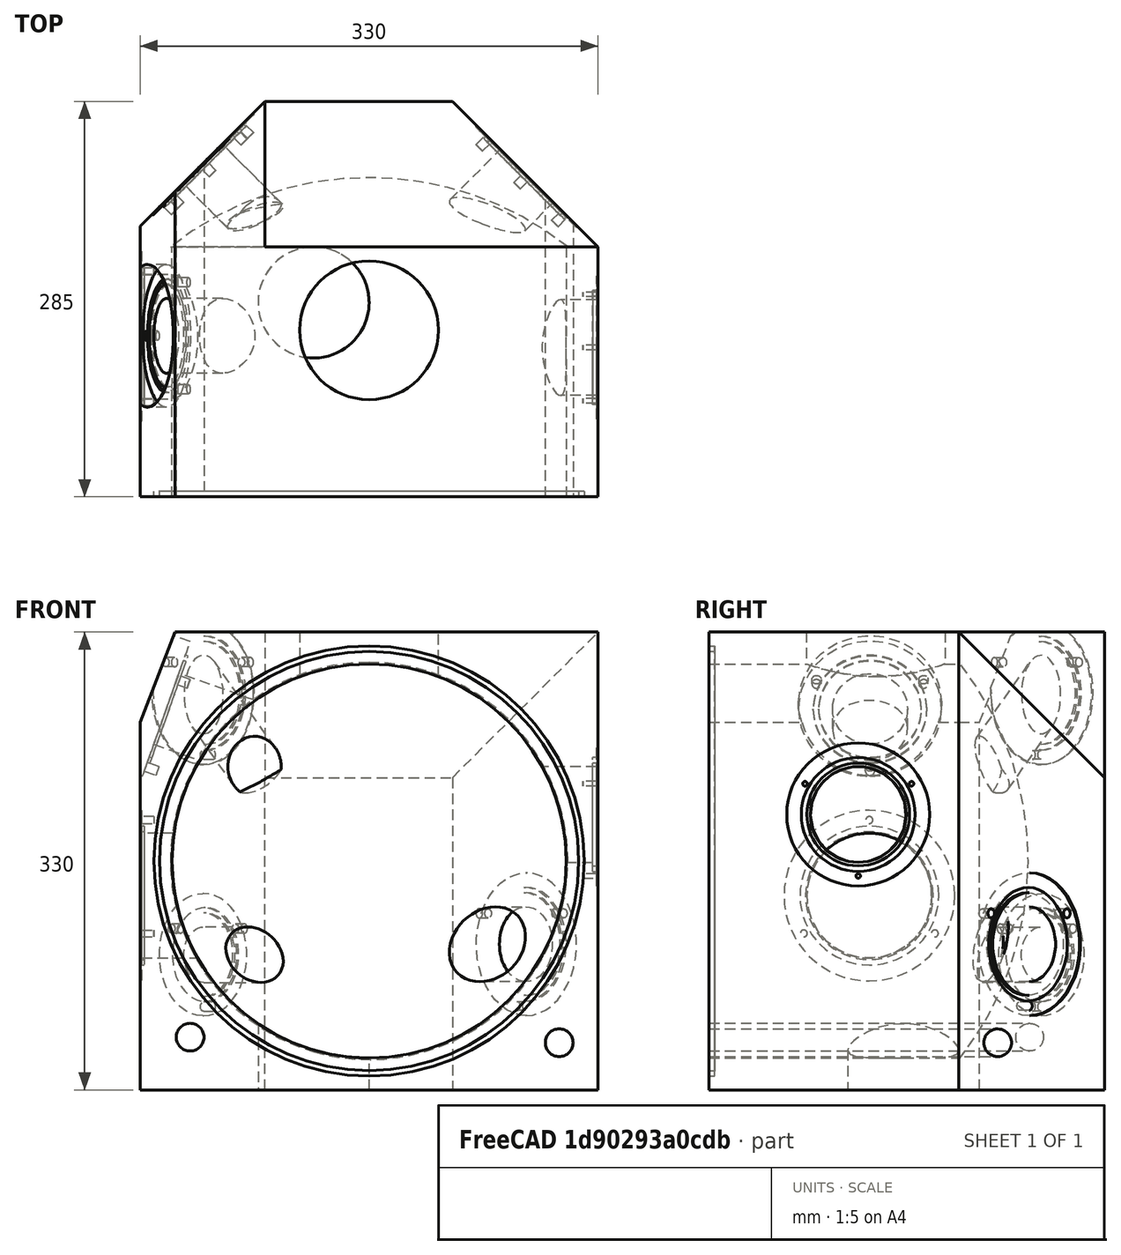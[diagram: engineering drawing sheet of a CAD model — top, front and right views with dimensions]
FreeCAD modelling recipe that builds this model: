
FCSTD DOCUMENT  (FreeCAD 0.20R)
Label: XL30MainChamberModel
License: All rights reserved
LicenseURL: http://en.wikipedia.org/wiki/All_rights_reserved
objects: Part::Cylinder×49, Part::Cut×21, Part::Compound×17, Part::MultiFuse×8, Part::Box×7, Part::Sphere×1
note: 103 computed .brp shape members not serialized (recipe doc carries the construction recipe); baked Part::Feature solids carry a one-line shape summary decoded from their .brp

FEATURE [Part::Box] Box  label="Würfel"
  AttacherType = Attacher::AttachEngine3D
  Height = 330
  Length = 330
  Width = 180
FEATURE [Part::Cylinder] Cylinder  label="Zylinder"
  Angle = 360
  AttacherType = Attacher::AttachEngine3D
  FirstAngle = 0
  Height = 180
  Placement = pos=(165,180,165) rot=(1,0,0;1.5708rad)
  Radius = 142
  SecondAngle = 0
FEATURE [Part::Cut] Cut
  Base = -> Box
  Tool = -> Cylinder
FEATURE [Part::Box] Box001  label="Würfel001"
  AttacherType = Attacher::AttachEngine3D
  Height = 50
  Length = 70
  Placement = pos=(0,0,265) rot=(0,-1,0;1.20428rad)
  Width = 180
FEATURE [Part::Cut] Cut001
  Base = -> Cut
  Tool = -> Box001
FEATURE [Part::Cylinder] Cylinder001  label="Flange100Right_Hole"
  Angle = 360
  AttacherType = Attacher::AttachEngine3D
  FirstAngle = 0
  Height = 50
  Placement = pos=(284,107.5,198.5) rot=(0,1,0;1.5708rad)
  Radius = 34.5
  SecondAngle = 0
FEATURE [Part::Cylinder] Cylinder002  label="Flange100Right_Recess"
  Angle = 360
  AttacherType = Attacher::AttachEngine3D
  FirstAngle = 0
  Height = 1
  Placement = pos=(329,107.5,198.5) rot=(0,1,0;1.5708rad)
  Radius = 51.5
  SecondAngle = 0
FEATURE [Part::Cylinder] Cylinder003  label="Zylinder001"
  Angle = 360
  AttacherType = Attacher::AttachEngine3D
  FirstAngle = 0
  Height = 3
  Radius = 41
  SecondAngle = 0
FEATURE [Part::Cylinder] Cylinder004  label="Zylinder002"
  Angle = 360
  AttacherType = Attacher::AttachEngine3D
  FirstAngle = 0
  Height = 3
  Radius = 37
  SecondAngle = 0
FEATURE [Part::Cut] Cut002
  Base = -> Cylinder003
  Placement = pos=(326,107.5,198.5) rot=(0,1,0;1.5708rad)
  Tool = -> Cylinder004
FEATURE [Part::Cylinder] Cylinder005  label="Zylinder003"
  Angle = 360
  AttacherType = Attacher::AttachEngine3D
  FirstAngle = 0
  Height = 10
  Placement = pos=(0,0,-44.3) rot=(0,1,0;1.5708rad)
  Radius = 1.65
  SecondAngle = 0
FEATURE [Part::Cylinder] Cylinder006  label="Zylinder004"
  Angle = 360
  AttacherType = Attacher::AttachEngine3D
  FirstAngle = 0
  Height = 10
  Placement = pos=(0,0,-44.3) rot=(0,1,0;1.5708rad)
  Radius = 1.65
  SecondAngle = 0
FEATURE [Part::Cylinder] Cylinder007  label="Zylinder005"
  Angle = 360
  AttacherType = Attacher::AttachEngine3D
  FirstAngle = 0
  Height = 10
  Placement = pos=(0,0,-44.3) rot=(0,1,0;1.5708rad)
  Radius = 1.65
  SecondAngle = 0
FEATURE [Part::Compound] Compound001
  Links = -> [Cylinder006]
  Placement = pos=(0,0,0) rot=(1,0,0;2.0944rad)
FEATURE [Part::Compound] Compound002
  Links = -> [Cylinder007]
  Placement = pos=(0,0,0) rot=(1,0,0;4.18879rad)
FEATURE [Part::Compound] Compound003  label="M4 holes flange right"
  Links = -> [Cylinder005,Compound001,Compound002]
  Placement = pos=(319,107.5,198.5) rot=(0,0,1;0rad)
FEATURE [Part::MultiFuse] Fusion
  Shapes = -> [Cylinder001,Cylinder002,Cut002,Compound003]
FEATURE [Part::Cut] Cut003
  Base = -> Cut001
  Tool = -> Fusion
FEATURE [Part::Cylinder] Cylinder008  label="Flange120LeftLow_Recess"
  Angle = 360
  AttacherType = Attacher::AttachEngine3D
  FirstAngle = 0
  Height = 1
  Placement = pos=(0,0,-1) rot=(0,0,1;0rad)
  Radius = 61.5
  SecondAngle = 0
FEATURE [Part::Cylinder] Cylinder009  label="Zylinder006"
  Angle = 360
  AttacherType = Attacher::AttachEngine3D
  FirstAngle = 0
  Height = 60
  Placement = pos=(0,0,-45) rot=(0,0,1;0rad)
  Radius = 45
  SecondAngle = 0
FEATURE [Part::Cylinder] Cylinder010  label="Zylinder007"
  Angle = 360
  AttacherType = Attacher::AttachEngine3D
  FirstAngle = 0
  Height = 2
  Placement = pos=(0,0,-3) rot=(0,0,1;0rad)
  Radius = 50
  SecondAngle = 0
FEATURE [Part::Cylinder] Cylinder011  label="Zylinder008"
  Angle = 360
  AttacherType = Attacher::AttachEngine3D
  FirstAngle = 0
  Height = 2
  Placement = pos=(0,0,-3) rot=(0,0,1;0rad)
  Radius = 46
  SecondAngle = 0
FEATURE [Part::Cut] Cut004
  Base = -> Cylinder010
  Tool = -> Cylinder011
FEATURE [Part::Cylinder] Cylinder012  label="Zylinder009"
  Angle = 360
  AttacherType = Attacher::AttachEngine3D
  FirstAngle = 0
  Height = 10
  Placement = pos=(54.5,0,-10) rot=(0,0,1;0rad)
  Radius = 2.5
  SecondAngle = 0
FEATURE [Part::Cylinder] Cylinder013  label="Zylinder010"
  Angle = 360
  AttacherType = Attacher::AttachEngine3D
  FirstAngle = 0
  Height = 10
  Placement = pos=(54.5,0,-10) rot=(0,0,1;0rad)
  Radius = 2.5
  SecondAngle = 0
FEATURE [Part::Cylinder] Cylinder015  label="Zylinder012"
  Angle = 360
  AttacherType = Attacher::AttachEngine3D
  FirstAngle = 0
  Height = 10
  Placement = pos=(54.5,0,-10) rot=(0,0,1;0rad)
  Radius = 2.5
  SecondAngle = 0
FEATURE [Part::Compound] Compound
  Links = -> [Cylinder013]
  Placement = pos=(0,0,0) rot=(0,0,1;2.0944rad)
FEATURE [Part::Compound] Compound004
  Links = -> [Cylinder015]
  Placement = pos=(0,0,0) rot=(0,0,1;4.18879rad)
FEATURE [Part::MultiFuse] Fusion001  label="Flange120LeftLow"
  Placement = pos=(0,115.5,140) rot=(0,-1,0;1.5708rad)
  Shapes = -> [Cylinder008,Cylinder009,Cut004,Cylinder012,Compound,Compound004]
FEATURE [Part::Cut] Cut005
  Base = -> Cut003
  Tool = -> Fusion001
FEATURE [Part::Cylinder] Cylinder016  label="Zylinder013"
  Angle = 360
  AttacherType = Attacher::AttachEngine3D
  FirstAngle = 0
  Height = 100
  Placement = pos=(0,0,0) rot=(0,1,0;1.5708rad)
  Radius = 27
  SecondAngle = 0
FEATURE [Part::Cylinder] Cylinder017  label="Zylinder014"
  Angle = 360
  AttacherType = Attacher::AttachEngine3D
  FirstAngle = 0
  Height = 100
  Placement = pos=(-99,0,0) rot=(0,1,0;1.5708rad)
  Radius = 51.5
  SecondAngle = 0
FEATURE [Part::Cylinder] Cylinder018  label="Zylinder015"
  Angle = 360
  AttacherType = Attacher::AttachEngine3D
  FirstAngle = 0
  Height = 2
  Radius = 41
  SecondAngle = 0
FEATURE [Part::Cylinder] Cylinder019  label="Zylinder016"
  Angle = 360
  AttacherType = Attacher::AttachEngine3D
  FirstAngle = 0
  Height = 2
  Radius = 37
  SecondAngle = 0
FEATURE [Part::Cut] Cut006
  Base = -> Cylinder018
  Placement = pos=(1,0,0) rot=(0,1,0;1.5708rad)
  Tool = -> Cylinder019
FEATURE [Part::Cylinder] Cylinder020  label="Zylinder017"
  Angle = 360
  AttacherType = Attacher::AttachEngine3D
  FirstAngle = 0
  Height = 10
  Placement = pos=(0,0,-44.5) rot=(0,1,0;1.5708rad)
  Radius = 3.3
  SecondAngle = 0
FEATURE [Part::Cylinder] Cylinder021  label="Zylinder018"
  Angle = 360
  AttacherType = Attacher::AttachEngine3D
  FirstAngle = 0
  Height = 10
  Placement = pos=(0,0,-44.5) rot=(0,1,0;1.5708rad)
  Radius = 3.3
  SecondAngle = 0
FEATURE [Part::Cylinder] Cylinder022  label="Zylinder019"
  Angle = 360
  AttacherType = Attacher::AttachEngine3D
  FirstAngle = 0
  Height = 10
  Placement = pos=(0,0,-44.5) rot=(0,1,0;1.5708rad)
  Radius = 3.3
  SecondAngle = 0
FEATURE [Part::Compound] Compound005
  Links = -> [Cylinder021]
  Placement = pos=(0,0,0) rot=(1,0,0;2.0944rad)
FEATURE [Part::Compound] Compound006
  Links = -> [Cylinder022]
  Placement = pos=(0,0,0) rot=(1,0,0;4.18879rad)
FEATURE [Part::MultiFuse] Fusion002  label="FlangeSEDetector"
  Placement = pos=(18,116,275) rot=(0,1,0;0.340339rad)
  Shapes = -> [Cylinder016,Cylinder017,Cut006,Cylinder020,Compound005,Compound006]
FEATURE [Part::Cut] Cut007
  Base = -> Cut005
  Tool = -> Fusion002
FEATURE [Part::Cylinder] Cylinder023  label="ODPHoleNoFlange"
  Angle = 360
  AttacherType = Attacher::AttachEngine3D
  FirstAngle = 0
  Height = 50
  Placement = pos=(125,140,0) rot=(0,0,1;0rad)
  Radius = 40
  SecondAngle = 0
FEATURE [Part::Cut] Cut008
  Base = -> Cut007
  Tool = -> Cylinder023
FEATURE [Part::Cylinder] Cylinder024  label="EGunHoleWithoutFlange"
  Angle = 360
  AttacherType = Attacher::AttachEngine3D
  FirstAngle = 0
  Height = 50
  Placement = pos=(165,120,280) rot=(0,0,1;0rad)
  Radius = 50
  SecondAngle = 0
FEATURE [Part::Cut] Cut009  label="FrontChamber"
  Base = -> Cut008
  Tool = -> Cylinder024
FEATURE [Part::Box] Box002  label="Würfel002"
  AttacherType = Attacher::AttachEngine3D
  Height = 330
  Length = 330
  Width = 105
FEATURE [Part::Box] Box003  label="Würfel003"
  AttacherType = Attacher::AttachEngine3D
  Height = 330
  Length = 150
  Placement = pos=(330,0,0) rot=(0,0,1;0.785398rad)
  Width = 200
FEATURE [Part::Box] Box004  label="Würfel004"
  AttacherType = Attacher::AttachEngine3D
  Height = 150
  Length = 240
  Placement = pos=(90,0,330) rot=(-1,0,0;0.785398rad)
  Width = 150
FEATURE [Part::Box] Box005  label="Würfel005"
  AttacherType = Attacher::AttachEngine3D
  Height = 330
  Length = 150
  Placement = pos=(0,15,0) rot=(0,0,1;0.785398rad)
  Width = 100
FEATURE [Part::Box] Box007  label="Würfel007"
  AttacherType = Attacher::AttachEngine3D
  Height = 50
  Length = 70
  Placement = pos=(0,0,265) rot=(0,-1,0;1.20428rad)
  Width = 180
FEATURE [Part::MultiFuse] Fusion003
  Shapes = -> [Box005,Box003,Box004,Box007]
FEATURE [Part::Cut] Cut010
  Base = -> Box002
  Placement = pos=(0,180,0) rot=(0,0,1;0rad)
  Tool = -> Fusion003
FEATURE [Part::Cylinder] Cylinder025  label="Zylinder020"
  Angle = 360
  AttacherType = Attacher::AttachEngine3D
  FirstAngle = 0
  Height = 100
  Placement = pos=(0,0,0) rot=(0,1,0;1.5708rad)
  Radius = 27
  SecondAngle = 0
FEATURE [Part::Cylinder] Cylinder026  label="Zylinder021"
  Angle = 360
  AttacherType = Attacher::AttachEngine3D
  FirstAngle = 0
  Height = 100
  Placement = pos=(-99,0,0) rot=(0,1,0;1.5708rad)
  Radius = 51.5
  SecondAngle = 0
FEATURE [Part::Cylinder] Cylinder027  label="Zylinder022"
  Angle = 360
  AttacherType = Attacher::AttachEngine3D
  FirstAngle = 0
  Height = 2
  Radius = 41
  SecondAngle = 0
FEATURE [Part::Cylinder] Cylinder028  label="Zylinder023"
  Angle = 360
  AttacherType = Attacher::AttachEngine3D
  FirstAngle = 0
  Height = 2
  Radius = 37
  SecondAngle = 0
FEATURE [Part::Cut] Cut011
  Base = -> Cylinder027
  Placement = pos=(1,0,0) rot=(0,1,0;1.5708rad)
  Tool = -> Cylinder028
FEATURE [Part::Cylinder] Cylinder029  label="Zylinder024"
  Angle = 360
  AttacherType = Attacher::AttachEngine3D
  FirstAngle = 0
  Height = 10
  Placement = pos=(0,0,-44.5) rot=(0,1,0;1.5708rad)
  Radius = 3.3
  SecondAngle = 0
FEATURE [Part::Cylinder] Cylinder030  label="Zylinder025"
  Angle = 360
  AttacherType = Attacher::AttachEngine3D
  FirstAngle = 0
  Height = 10
  Placement = pos=(0,0,-44.5) rot=(0,1,0;1.5708rad)
  Radius = 3.3
  SecondAngle = 0
FEATURE [Part::Compound] Compound007
  Links = -> [Cylinder030]
  Placement = pos=(0,0,0) rot=(1,0,0;2.0944rad)
FEATURE [Part::Cylinder] Cylinder031  label="Zylinder026"
  Angle = 360
  AttacherType = Attacher::AttachEngine3D
  FirstAngle = 0
  Height = 10
  Placement = pos=(0,0,-44.5) rot=(0,1,0;1.5708rad)
  Radius = 3.3
  SecondAngle = 0
FEATURE [Part::Compound] Compound008
  Links = -> [Cylinder031]
  Placement = pos=(0,0,0) rot=(1,0,0;4.18879rad)
FEATURE [Part::MultiFuse] Fusion004  label="BSEFlange"
  Placement = pos=(278.7,231.3,105) rot=(0,0,1;3.92699rad)
  Shapes = -> [Cylinder025,Cylinder026,Cut011,Cylinder029,Compound007,Compound008]
FEATURE [Part::Compound] Compound009  label="BSEFlange1"
  Links = -> [Fusion004]
FEATURE [Part::Cut] Cut012
  Base = -> Cut010
  Tool = -> Compound009
FEATURE [Part::Cylinder] Cylinder032  label="Zylinder027"
  Angle = 360
  AttacherType = Attacher::AttachEngine3D
  FirstAngle = 0
  Height = 100
  Placement = pos=(0,0,0) rot=(0,1,0;1.5708rad)
  Radius = 20
  SecondAngle = 0
FEATURE [Part::Cylinder] Cylinder033  label="Zylinder028"
  Angle = 360
  AttacherType = Attacher::AttachEngine3D
  FirstAngle = 0
  Height = 100
  Placement = pos=(-99,0,0) rot=(0,1,0;1.5708rad)
  Radius = 44
  SecondAngle = 0
FEATURE [Part::Cylinder] Cylinder034  label="Zylinder029"
  Angle = 360
  AttacherType = Attacher::AttachEngine3D
  FirstAngle = 0
  Height = 2
  Radius = 33.8
  SecondAngle = 0
FEATURE [Part::Cylinder] Cylinder035  label="Zylinder030"
  Angle = 360
  AttacherType = Attacher::AttachEngine3D
  FirstAngle = 0
  Height = 2
  Radius = 30
  SecondAngle = 0
FEATURE [Part::Cut] Cut013
  Base = -> Cylinder034
  Placement = pos=(1,0,0) rot=(0,1,0;1.5708rad)
  Tool = -> Cylinder035
FEATURE [Part::Cylinder] Cylinder036  label="Zylinder031"
  Angle = 360
  AttacherType = Attacher::AttachEngine3D
  FirstAngle = 0
  Height = 10
  Placement = pos=(0,0,-37.5) rot=(0,1,0;1.5708rad)
  Radius = 3.3
  SecondAngle = 0
FEATURE [Part::Cylinder] Cylinder037  label="Zylinder032"
  Angle = 360
  AttacherType = Attacher::AttachEngine3D
  FirstAngle = 0
  Height = 10
  Placement = pos=(0,0,-37.5) rot=(0,1,0;1.5708rad)
  Radius = 3.3
  SecondAngle = 0
FEATURE [Part::Compound] Compound010
  Links = -> [Cylinder037]
  Placement = pos=(0,0,0) rot=(1,0,0;2.0944rad)
FEATURE [Part::Cylinder] Cylinder038  label="Zylinder033"
  Angle = 360
  AttacherType = Attacher::AttachEngine3D
  FirstAngle = 0
  Height = 10
  Placement = pos=(0,0,-37.5) rot=(0,1,0;1.5708rad)
  Radius = 3.3
  SecondAngle = 0
FEATURE [Part::Compound] Compound011
  Links = -> [Cylinder038]
  Placement = pos=(0,0,0) rot=(1,0,0;4.18879rad)
FEATURE [Part::MultiFuse] Fusion005  label="BSEFlange003"
  Placement = pos=(0,0,0) rot=(0,0,-1;0.785398rad)
  Shapes = -> [Cylinder032,Cylinder033,Cut013,Cylinder036,Compound010,Compound011]
FEATURE [Part::Compound] Compound012  label="SideFlangeBack2Low"
  Links = -> [Fusion005]
  Placement = pos=(45,240,97.5) rot=(0,0,1;0rad)
FEATURE [Part::Cut] Cut014
  Base = -> Cut012
  Tool = -> Compound012
FEATURE [Part::Cylinder] Cylinder039  label="Zylinder034"
  Angle = 360
  AttacherType = Attacher::AttachEngine3D
  FirstAngle = 0
  Height = 110
  Placement = pos=(-20,0,20) rot=(0,1,0;2.35619rad)
  Radius = 20
  SecondAngle = 0
FEATURE [Part::Cylinder] Cylinder040  label="Zylinder035"
  Angle = 360
  AttacherType = Attacher::AttachEngine3D
  FirstAngle = 0
  Height = 100
  Placement = pos=(-99,0,0) rot=(0,1,0;1.5708rad)
  Radius = 51.5
  SecondAngle = 0
FEATURE [Part::Cylinder] Cylinder041  label="Zylinder036"
  Angle = 360
  AttacherType = Attacher::AttachEngine3D
  FirstAngle = 0
  Height = 2
  Radius = 41
  SecondAngle = 0
FEATURE [Part::Cylinder] Cylinder042  label="Zylinder037"
  Angle = 360
  AttacherType = Attacher::AttachEngine3D
  FirstAngle = 0
  Height = 2
  Radius = 37
  SecondAngle = 0
FEATURE [Part::Cut] Cut015
  Base = -> Cylinder041
  Placement = pos=(1,0,0) rot=(0,1,0;1.5708rad)
  Tool = -> Cylinder042
FEATURE [Part::Cylinder] Cylinder043  label="Zylinder038"
  Angle = 360
  AttacherType = Attacher::AttachEngine3D
  FirstAngle = 0
  Height = 10
  Placement = pos=(0,0,-44.5) rot=(0,1,0;1.5708rad)
  Radius = 3.3
  SecondAngle = 0
FEATURE [Part::Cylinder] Cylinder044  label="Zylinder039"
  Angle = 360
  AttacherType = Attacher::AttachEngine3D
  FirstAngle = 0
  Height = 10
  Placement = pos=(0,0,-44.5) rot=(0,1,0;1.5708rad)
  Radius = 3.3
  SecondAngle = 0
FEATURE [Part::Compound] Compound013
  Links = -> [Cylinder044]
  Placement = pos=(0,0,0) rot=(1,0,0;2.0944rad)
FEATURE [Part::Cylinder] Cylinder045  label="Zylinder040"
  Angle = 360
  AttacherType = Attacher::AttachEngine3D
  FirstAngle = 0
  Height = 10
  Placement = pos=(0,0,-44.5) rot=(0,1,0;1.5708rad)
  Radius = 3.3
  SecondAngle = 0
FEATURE [Part::Compound] Compound014
  Links = -> [Cylinder045]
  Placement = pos=(0,0,0) rot=(1,0,0;4.18879rad)
FEATURE [Part::MultiFuse] Fusion006  label="BSEFlange005"
  Placement = pos=(0,0,286) rot=(0,0,-1;0.785398rad)
  Shapes = -> [Cylinder039,Cylinder040,Cut015,Cylinder043,Compound013,Compound014]
FEATURE [Part::Compound] Compound015  label="BackTopFlange100"
  Links = -> [Fusion006]
  Placement = pos=(45,240,0) rot=(0,0,1;0rad)
FEATURE [Part::Cut] Cut016  label="BackChamber01"
  Base = -> Cut014
  Tool = -> Compound015
FEATURE [Part::Cylinder] Cylinder046  label="Zylinder041"
  Angle = 360
  AttacherType = Attacher::AttachEngine3D
  FirstAngle = 0
  Height = 800
  Placement = pos=(36,500,38) rot=(1,0,0;1.5708rad)
  Radius = 10
  SecondAngle = 0
FEATURE [Part::Cylinder] Cylinder047  label="Zylinder042"
  Angle = 360
  AttacherType = Attacher::AttachEngine3D
  FirstAngle = 0
  Height = 800
  Placement = pos=(302,500,34) rot=(1,0,0;1.5708rad)
  Radius = 10
  SecondAngle = 0
FEATURE [Part::Compound] Compound016
  Links = -> [Cylinder047,Cylinder046]
FEATURE [Part::Sphere] Sphere  label="Kugel"
  Angle1 = -90
  Angle2 = 90
  Angle3 = 360
  AttacherType = Attacher::AttachEngine3D
  Placement = pos=(165,0,165) rot=(0,0,1;0rad)
  Radius = 230
FEATURE [Part::Cut] Cut017
  Base = -> Cut016
  Tool = -> Sphere
FEATURE [Part::MultiFuse] Fusion007
  Shapes = -> [Cut009,Cut017]
FEATURE [Part::Cut] Cut018
  Base = -> Fusion007
  Tool = -> Compound016
FEATURE [Part::Cylinder] Cylinder048  label="Zylinder043"
  Angle = 360
  AttacherType = Attacher::AttachEngine3D
  FirstAngle = 0
  Height = 4
  Radius = 155
  SecondAngle = 0
FEATURE [Part::Cylinder] Cylinder049  label="Zylinder044"
  Angle = 360
  AttacherType = Attacher::AttachEngine3D
  FirstAngle = 0
  Height = 4
  Radius = 151
  SecondAngle = 0
FEATURE [Part::Cut] Cut019
  Base = -> Cylinder048
  Placement = pos=(165,4,165) rot=(1,0,0;1.5708rad)
  Tool = -> Cylinder049
FEATURE [Part::Cut] Cut020  label="MainChamberModel"
  Base = -> Cut018
  Tool = -> Cut019
